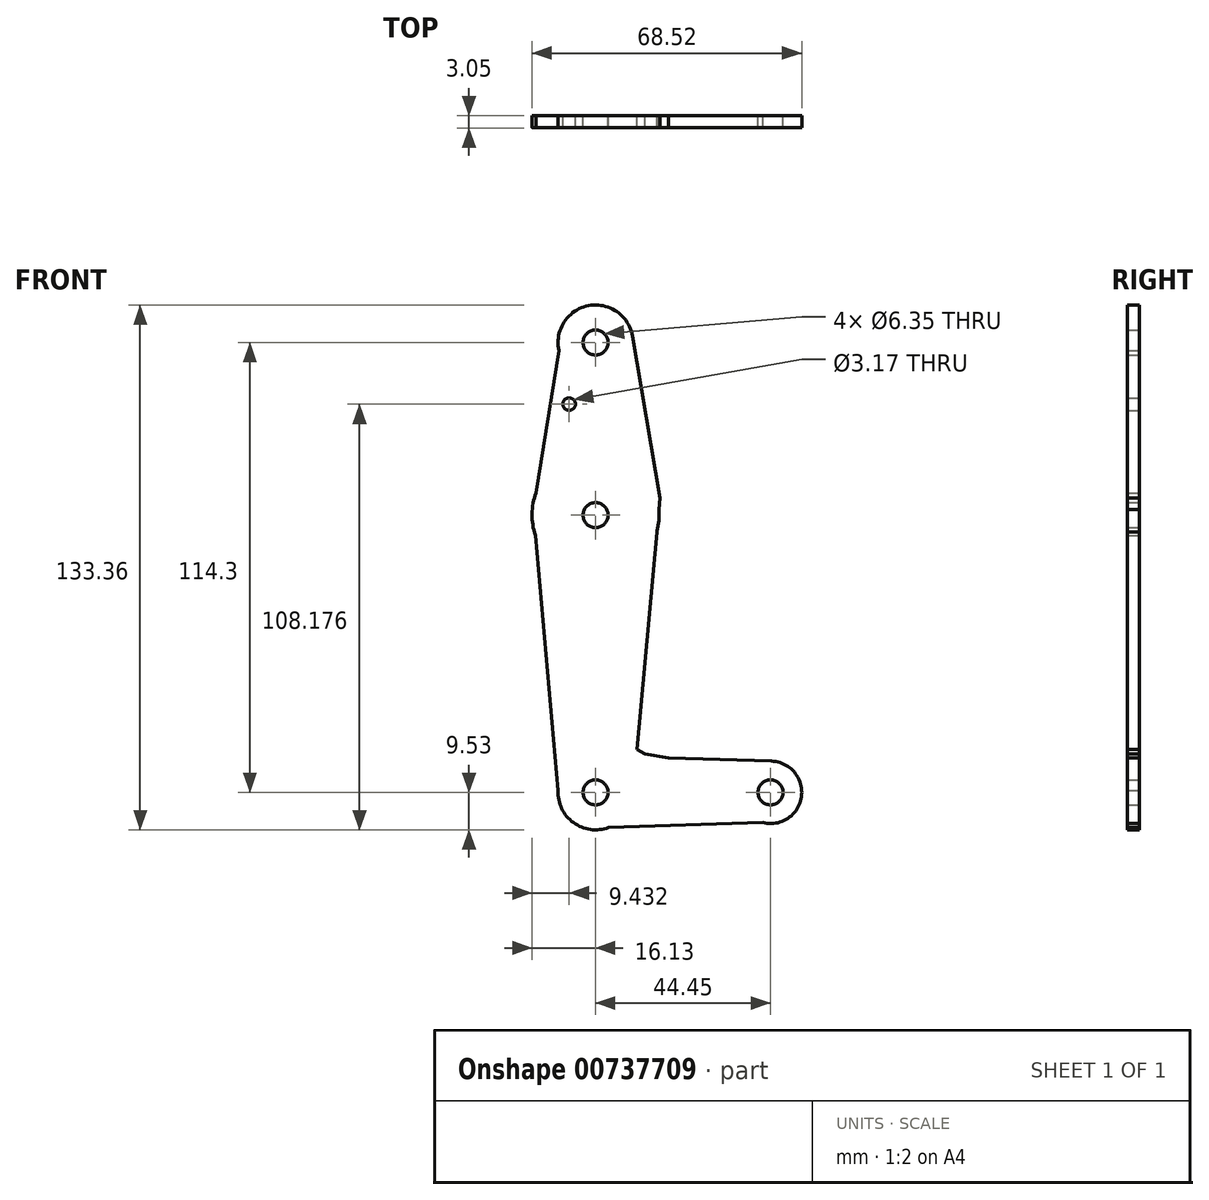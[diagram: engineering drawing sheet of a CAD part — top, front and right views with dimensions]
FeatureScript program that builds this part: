
annotation { "Feature Type Name" : "Feature", "Feature Type Description" : "" }
export const myFeature = defineFeature(function(context is Context, id is Id, definition is map)
    precondition{}
    {
        {
            var Q0;
            Q0=qCreatedBy(makeId("Front.planeOp"),FACE);
            var sketch = newSketch(context, id + "F0", { "sketchPlane" : qUnion([Q0])});
            skLineSegment(sketch, "E0", {"start": v(0, 0) * mm, "end": v(0, 114.3) * mm, "construction": true});
            skLineSegment(sketch, "E1", {"start": v(3.66, 0) * mm, "end": v(44.45, 0) * mm, "construction": true});
            skArc(sketch, "E2", {"start": v(-8.22, 119.1) * mm, "mid": v(-9.4, 115.8) * mm, "end": v(-9.31, 112.3) * mm, "construction": true});
            skArc(sketch, "E3", {"start": v(-15.37, 74.4) * mm, "mid": v(-15.87, 70.52) * mm, "end": v(-15.41, 66.63) * mm, "construction": true});
            skLineSegment(sketch, "E4", {"start": v(10.45, 10.2) * mm, "end": v(10.52, 10.89) * mm});
            skLineSegment(sketch, "E5", {"start": v(16.34, 74.79) * mm, "end": v(9.4, 115.89) * mm});
            skLineSegment(sketch, "E6", {"start": v(-9.28, -2.14) * mm, "end": v(-15.84, 71.45) * mm});
            skLineSegment(sketch, "E7", {"start": v(-15.84, 71.45) * mm, "end": v(-9.31, 112.3) * mm});
            skCircle(sketch, "E8", {"center": v(0, 70.43) * mm, "radius": 16.13 * mm});
            skCircle(sketch, "E9", {"center": v(0, 114.3) * mm, "radius": 9.53 * mm});
            skArc(sketch, "E10.trimOffspring", {"start": v(-9.51, 0.46) * mm, "mid": v(-9.49, -0.85) * mm, "end": v(-9.28, -2.14) * mm, "construction": true});
            skCircle(sketch, "E11", {"center": v(0, 0) * mm, "radius": 9.53 * mm});
            skCircle(sketch, "E12", {"center": v(44.45, 0) * mm, "radius": 7.94 * mm});
            skLineSegment(sketch, "E13", {"start": v(-2.77, -9.11) * mm, "end": v(42.47, -7.69) * mm});
            skCircle(sketch, "E14", {"center": v(0, 114.3) * mm, "radius": 3.18 * mm});
            skCircle(sketch, "E15", {"center": v(-6.7, 98.65) * mm, "radius": 1.59 * mm});
            skCircle(sketch, "E16", {"center": v(0, 70.43) * mm, "radius": 3.18 * mm});
            skCircle(sketch, "E17", {"center": v(0, 0) * mm, "radius": 3.18 * mm});
            skCircle(sketch, "E18", {"center": v(44.45, 0) * mm, "radius": 3.18 * mm});
            skLineSegment(sketch, "E19", {"start": v(18.6, 8.72) * mm, "end": v(12.6, 9.81) * mm});
            skLineSegment(sketch, "E20", {"start": v(10.45, 10.2) * mm, "end": v(11.85, 25.5) * mm});
            skLineSegment(sketch, "E21.trimOffspring", {"start": v(18.6, 8.72) * mm, "end": v(44.69, 7.93) * mm});
            skLineSegment(sketch, "E22.trimOffspring", {"start": v(11.07, 17.01) * mm, "end": v(16.34, 74.79) * mm});
            skLineSegment(sketch, "E23", {"start": v(12.6, 9.81) * mm, "end": v(10.52, 10.89) * mm});
            skSolve(sketch);
        }
        {
            var Q0;
            Q0 = qSketchRegion(id + "F0", true);
            extrude(context, id + "F1", {"entities" : qUnion([Q0]), "depth" : 3.05 * mm, "offsetDistance" : 25.4 * mm});
        }
    });
